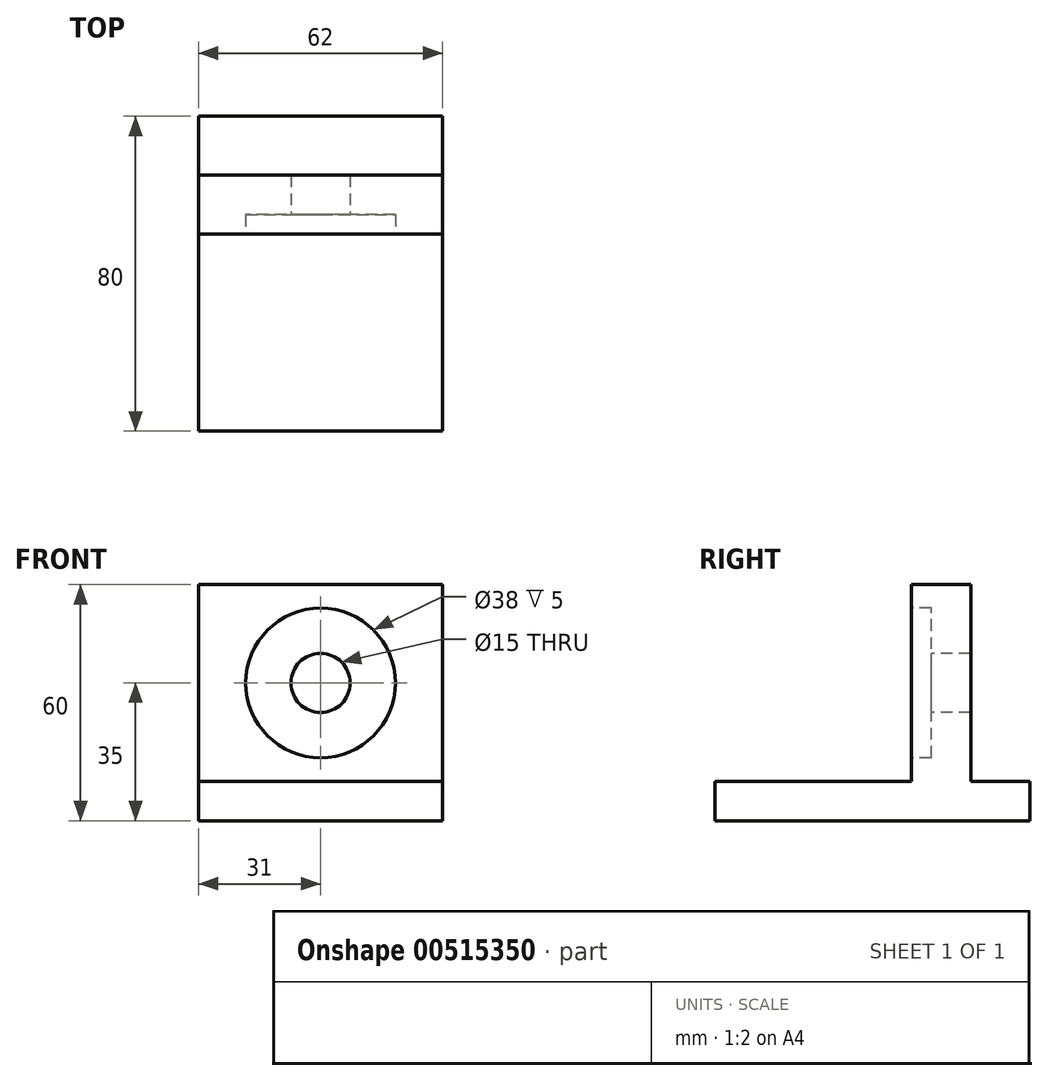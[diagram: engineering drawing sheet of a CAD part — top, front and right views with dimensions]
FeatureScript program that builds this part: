
annotation { "Feature Type Name" : "Feature", "Feature Type Description" : "" }
export const myFeature = defineFeature(function(context is Context, id is Id, definition is map)
    precondition{}
    {
        {
            var Q0;
            Q0=qCreatedBy(makeId("Top.planeOp"),FACE);
            var sketch = newSketch(context, id + "F0", { "sketchPlane" : qUnion([Q0])});
            skLineSegment(sketch, "E0.bottom", {"start": v(31, -40) * mm, "end": v(-31, -40) * mm});
            skLineSegment(sketch, "E0.top", {"start": v(31, 40) * mm, "end": v(-31, 40) * mm});
            skLineSegment(sketch, "E0.left", {"start": v(31, -40) * mm, "end": v(31, 40) * mm});
            skLineSegment(sketch, "E0.right", {"start": v(-31, -40) * mm, "end": v(-31, 40) * mm});
            skPoint(sketch, "E0.middle", {"position": v(0, 0) * mm});
            skLineSegment(sketch, "E1", {"start": v(-31, 25) * mm, "end": v(31, 25) * mm});
            skLineSegment(sketch, "E2", {"start": v(31, 10) * mm, "end": v(-31, 10) * mm});
            skSolve(sketch);
        }
        {
            var Q0;
            {var subQ0=sQuery(id+"F0.wireOp",EDGE,"E1");Q0=makeQuery(id+"F0.imprint","IMPRINT",FACE,{"disambiguationData":[TD([[makeQuery(id+"F0.imprint","IMPRINT",EDGE,{"derivedFrom":subQ0}),-1.0]])]});}
            extrude(context, id + "F1", {"entities" : qUnion([Q0]), "depth" : 60 * mm, "offsetDistance" : 25 * mm});
        }
        {
            var Q0;
            {var subQ0=sQuery(id+"F0.wireOp",EDGE,"E0.top");Q0=makeQuery(id+"F0.imprint","IMPRINT",FACE,{"disambiguationData":[TD([[makeQuery(id+"F0.imprint","IMPRINT",EDGE,{"derivedFrom":subQ0}),1.0]])]});}
            var Q1;
            {var subQ0=sQuery(id+"F0.wireOp",EDGE,"E0.bottom");Q1=makeQuery(id+"F0.imprint","IMPRINT",FACE,{"disambiguationData":[TD([[makeQuery(id+"F0.imprint","IMPRINT",EDGE,{"derivedFrom":subQ0}),-1.0]])]});}
            extrude(context, id + "F2", {"entities" : qUnion([Q0, Q1]), "operationType" : NewBodyOperationType.ADD, "depth" : 10 * mm, "offsetDistance" : 25 * mm});
        }
        {
            var Q0;
            Q0=makeQuery(id+"F1.opExtrude","SWEPT_FACE",FACE,{"disambiguationData":[OSD([sQuery(id+"F0.wireOp",EDGE,"E2")])]});
            var sketch = newSketch(context, id + "F3", { "sketchPlane" : qUnion([Q0])});
            skCircle(sketch, "E3", {"center": v(0, 35) * mm, "radius": 19 * mm});
            skSolve(sketch);
        }
        {
            var Q0;
            Q0=makeQuery(id+"F3.imprint","IMPRINT",FACE,{"disambiguationData":[TD([[makeQuery(id+"F3.imprint","IMPRINT",EDGE,{"derivedFrom":sQuery(id+"F3.wireOp",EDGE,"E3")}),1.0]])]});
            extrude(context, id + "F4", {"entities" : qUnion([Q0]), "operationType" : NewBodyOperationType.REMOVE, "oppositeDirection" : true, "depth" : 5 * mm, "offsetDistance" : 25 * mm});
        }
        {
            var Q0;
            Q0=makeQuery(id+"F4.boolean.opBoolean","COPY",FACE,{"derivedFrom":makeQuery(id+"F4.opExtrude","CAP_FACE",FACE,{"disambiguationData":[OSD([sQuery(id+"F3.wireOp",EDGE,"E3")])],"isStart":false})});
            var sketch = newSketch(context, id + "F5", { "sketchPlane" : qUnion([Q0])});
            skCircle(sketch, "E4", {"center": v(0, 35) * mm, "radius": 7.5 * mm});
            skSolve(sketch);
        }
        {
            var Q0;
            Q0=makeQuery(id+"F5.imprint","IMPRINT",FACE,{"disambiguationData":[TD([[makeQuery(id+"F5.imprint","IMPRINT",EDGE,{"derivedFrom":sQuery(id+"F5.wireOp",EDGE,"E4")}),1.0]])]});
            extrude(context, id + "F6", {"entities" : qUnion([Q0]), "operationType" : NewBodyOperationType.REMOVE, "endBound" : BoundingType.THROUGH_ALL, "oppositeDirection" : true, "depth" : 25 * mm, "offsetDistance" : 25 * mm});
        }
    });
